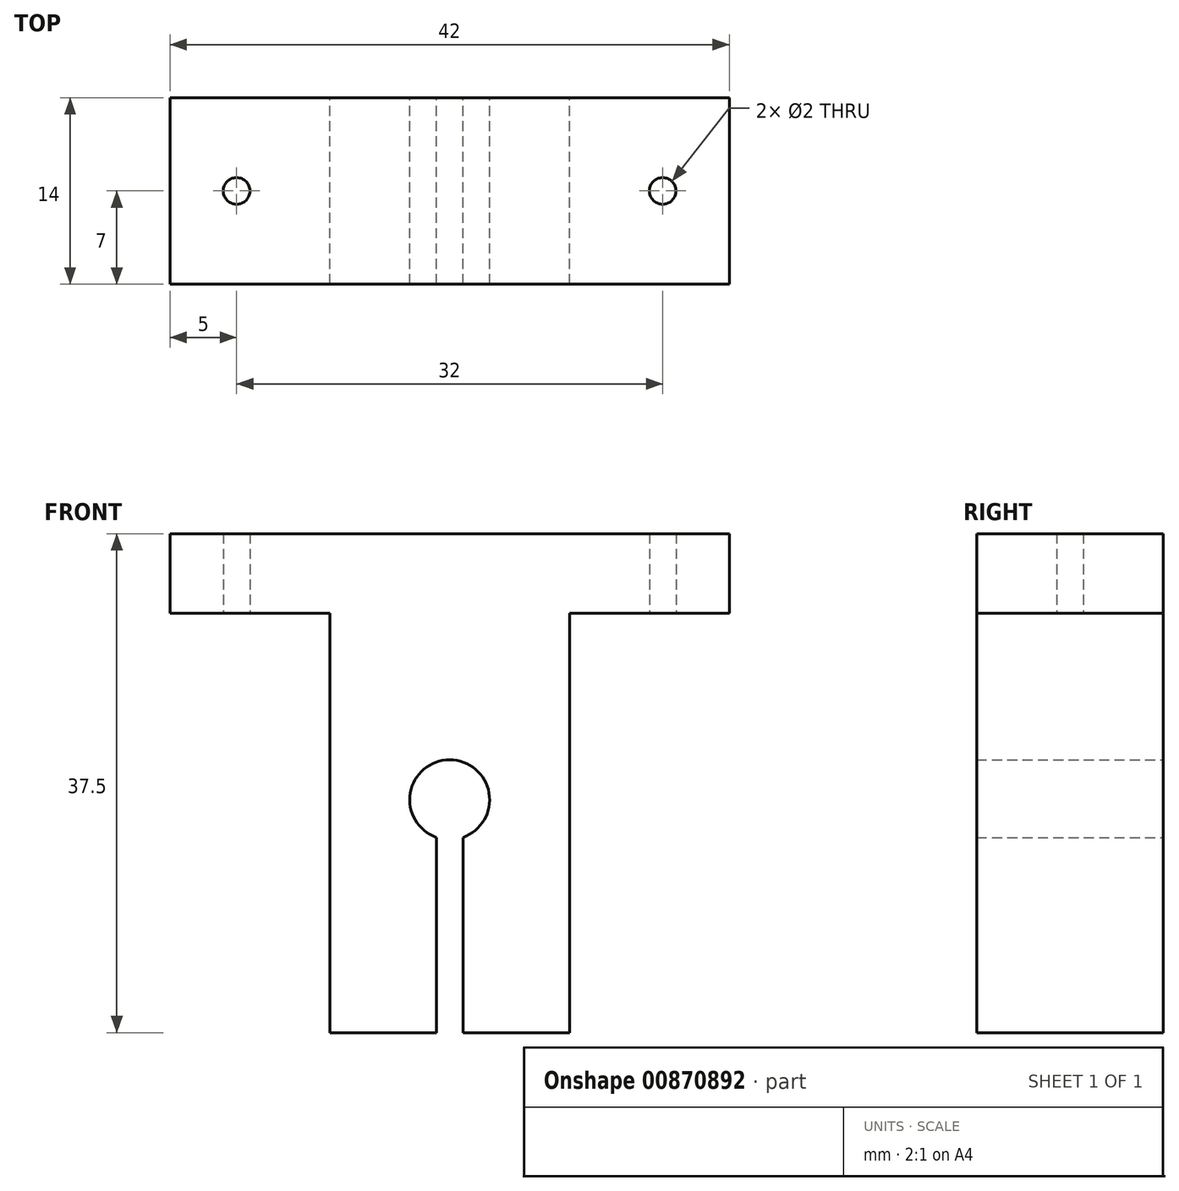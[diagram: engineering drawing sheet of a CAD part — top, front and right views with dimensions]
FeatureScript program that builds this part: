
annotation { "Feature Type Name" : "Feature", "Feature Type Description" : "" }
export const myFeature = defineFeature(function(context is Context, id is Id, definition is map)
    precondition{}
    {
        {
            var Q0;
            Q0=qCreatedBy(makeId("Front.planeOp"),FACE);
            var sketch = newSketch(context, id + "F0", { "sketchPlane" : qUnion([Q0])});
            skLineSegment(sketch, "E0", {"start": v(-21, 20) * mm, "end": v(21, 20) * mm});
            skPoint(sketch, "E1", {"position": v(0, 20) * mm});
            skCircle(sketch, "E2", {"center": v(0, 0) * mm, "radius": 3 * mm});
            skLineSegment(sketch, "E3", {"start": v(-21, 20) * mm, "end": v(-21, 14) * mm});
            skLineSegment(sketch, "E4", {"start": v(21, 20) * mm, "end": v(21, 14) * mm});
            skLineSegment(sketch, "E5", {"start": v(-9, -17.5) * mm, "end": v(9, -17.5) * mm});
            skPoint(sketch, "E6", {"position": v(0, -17.5) * mm});
            skLineSegment(sketch, "E7", {"start": v(-21, 14) * mm, "end": v(-9, 14) * mm});
            skLineSegment(sketch, "E8", {"start": v(-9, 14) * mm, "end": v(-9, -17.5) * mm});
            skLineSegment(sketch, "E9", {"start": v(9, -17.5) * mm, "end": v(9, 14) * mm});
            skLineSegment(sketch, "E10", {"start": v(9, 14) * mm, "end": v(21, 14) * mm});
            skSolve(sketch);
        }
        {
            var Q0;
            Q0=makeQuery(id+"F0.imprint","IMPRINT",FACE,{"disambiguationData":[TD([[makeQuery(id+"F0.imprint","IMPRINT",EDGE,{"derivedFrom":sQuery(id+"F0.wireOp",EDGE,"E0")}),-1.0]])]});
            extrude(context, id + "F1", {"entities" : qUnion([Q0]), "depth" : 14 * mm, "offsetDistance" : 25 * mm});
        }
        {
            var Q0;
            Q0=qCreatedBy(makeId("Front.planeOp"),FACE);
            var sketch = newSketch(context, id + "F2", { "sketchPlane" : qUnion([Q0])});
            skPoint(sketch, "E11", {"position": v(0, -17.5) * mm});
            skLineSegment(sketch, "E12", {"start": v(1, -17.5) * mm, "end": v(-1, -17.5) * mm});
            skCircle(sketch, "E13", {"center": v(0, 0) * mm, "radius": 3 * mm});
            skLineSegment(sketch, "E14", {"start": v(-1, -17.5) * mm, "end": v(-1, -2.83) * mm});
            skLineSegment(sketch, "E15", {"start": v(1, -17.5) * mm, "end": v(1, -2.83) * mm});
            skSolve(sketch);
        }
        {
            var Q0;
            Q0=makeQuery(id+"F2.imprint","IMPRINT",FACE,{"disambiguationData":[TD([[makeQuery(id+"F2.imprint","IMPRINT",EDGE,{"derivedFrom":sQuery(id+"F2.wireOp",EDGE,"E12")}),-1.0]])]});
            extrude(context, id + "F3", {"entities" : qUnion([Q0]), "operationType" : NewBodyOperationType.REMOVE, "depth" : 25 * mm, "offsetDistance" : 25 * mm});
        }
        {
            var Q0;
            Q0=qCreatedBy(makeId("Top.planeOp"),FACE);
            var sketch = newSketch(context, id + "F4", { "sketchPlane" : qUnion([Q0])});
            skPoint(sketch, "E16", {"position": v(21, -7) * mm});
            skLineSegment(sketch, "E17", {"start": v(16, -7) * mm, "end": v(-16, -7) * mm});
            skCircle(sketch, "E18", {"center": v(16, -7) * mm, "radius": 1 * mm});
            skCircle(sketch, "E19", {"center": v(-16, -7) * mm, "radius": 1 * mm});
            skSolve(sketch);
        }
        {
            var Q0;
            Q0 = qSketchRegion(id + "F4", true);
            extrude(context, id + "F5", {"entities" : qUnion([Q0]), "operationType" : NewBodyOperationType.REMOVE, "endBound" : BoundingType.THROUGH_ALL, "depth" : 25 * mm, "offsetDistance" : 25 * mm});
        }
    });
